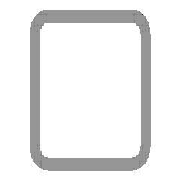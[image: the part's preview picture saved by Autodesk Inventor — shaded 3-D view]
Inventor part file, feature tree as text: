
AUTODESK INVENTOR PART (.ipt)
format: ipt  version: 2025 (Build 290162010, 162A)  size: 142,336 bytes
history: native  units: mm (DEFAULTED — no unit token found)
features: other x4, sketch x1, plane x1
ambient origin geometry x8: Origin, YZ Plane, XZ Plane, XY Plane, X Axis, Y Axis, Z Axis, Center Point
bodies: Solid1 (feature_tree), Body (feature_tree)
feature tree (6):
  parser-record x1  (decoder bookkeeping rows leaked as tree rows — omitted from the tree; the rows remain in map.json)
  other  "Driven Length"
  other  "Start Plane"
  other  "End Plane"
  sketch  "Sketch3"  dims[d3=635.0mm d4=0.0mm d7=4.0mm d9=40.0mm d11=40.0mm d12=2.0mm d13=50.0mm d14=685.0mm d15=20.0mm d16=20.0mm d17=90.0deg d18=635.0mm]
  plane  "Work Plane3"
